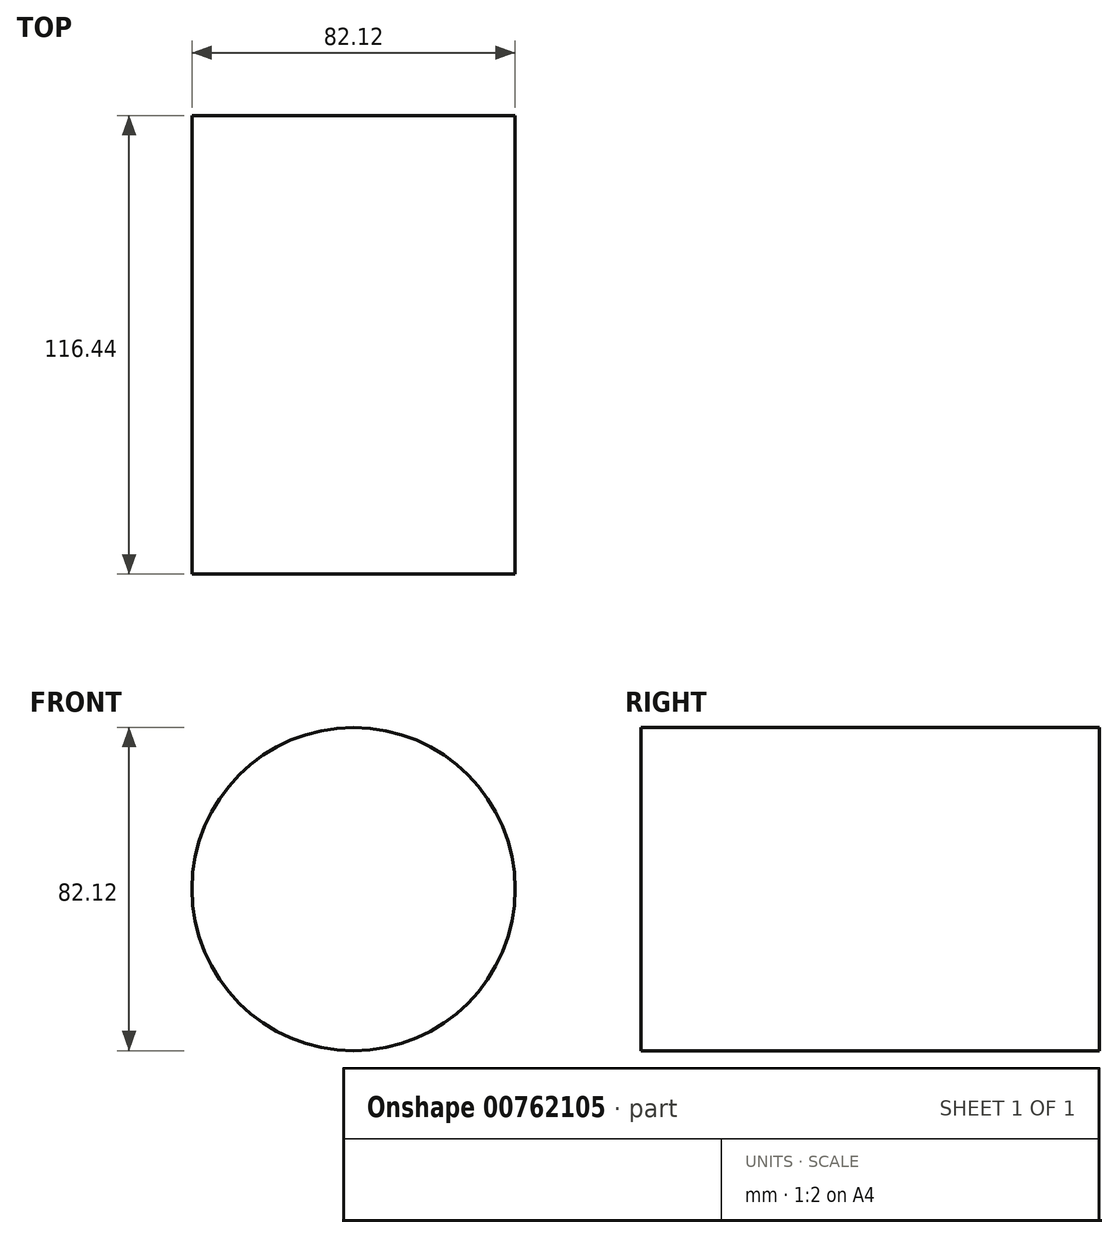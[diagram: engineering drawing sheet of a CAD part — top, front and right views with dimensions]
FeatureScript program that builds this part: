
annotation { "Feature Type Name" : "Feature", "Feature Type Description" : "" }
export const myFeature = defineFeature(function(context is Context, id is Id, definition is map)
    precondition{}
    {
        {
            var Q0;
            Q0=qCreatedBy(makeId("Right.planeOp"),FACE);
            var sketch = newSketch(context, id + "F0", { "sketchPlane" : qUnion([Q0])});
            skLineSegment(sketch, "E0.bottom", {"start": v(-62.97, 0) * mm, "end": v(53.47, 0) * mm});
            skLineSegment(sketch, "E0.top", {"start": v(-62.97, 41.06) * mm, "end": v(53.47, 41.06) * mm});
            skLineSegment(sketch, "E0.left", {"start": v(-62.97, 0) * mm, "end": v(-62.97, 41.06) * mm});
            skLineSegment(sketch, "E0.right", {"start": v(53.47, 0) * mm, "end": v(53.47, 41.06) * mm});
            skSolve(sketch);
        }
        {
            var Q0;
            Q0=makeQuery(id+"F0.imprint","IMPRINT",FACE,{"disambiguationData":[TD([[makeQuery(id+"F0.imprint","IMPRINT",EDGE,{"derivedFrom":sQuery(id+"F0.wireOp",EDGE,"E0.bottom")}),1.0]])]});
            var Q1;
            Q1=sQuery(id+"F0.wireOp",EDGE,"E0.bottom");
            revolve(context, id + "F1", {"surfaceOperationType" : NewSurfaceOperationType.NEW, "entities" : qUnion([Q0]), "axis" : qUnion([Q1]), "revolveType" : RevolveType.FULL});
        }
    });
